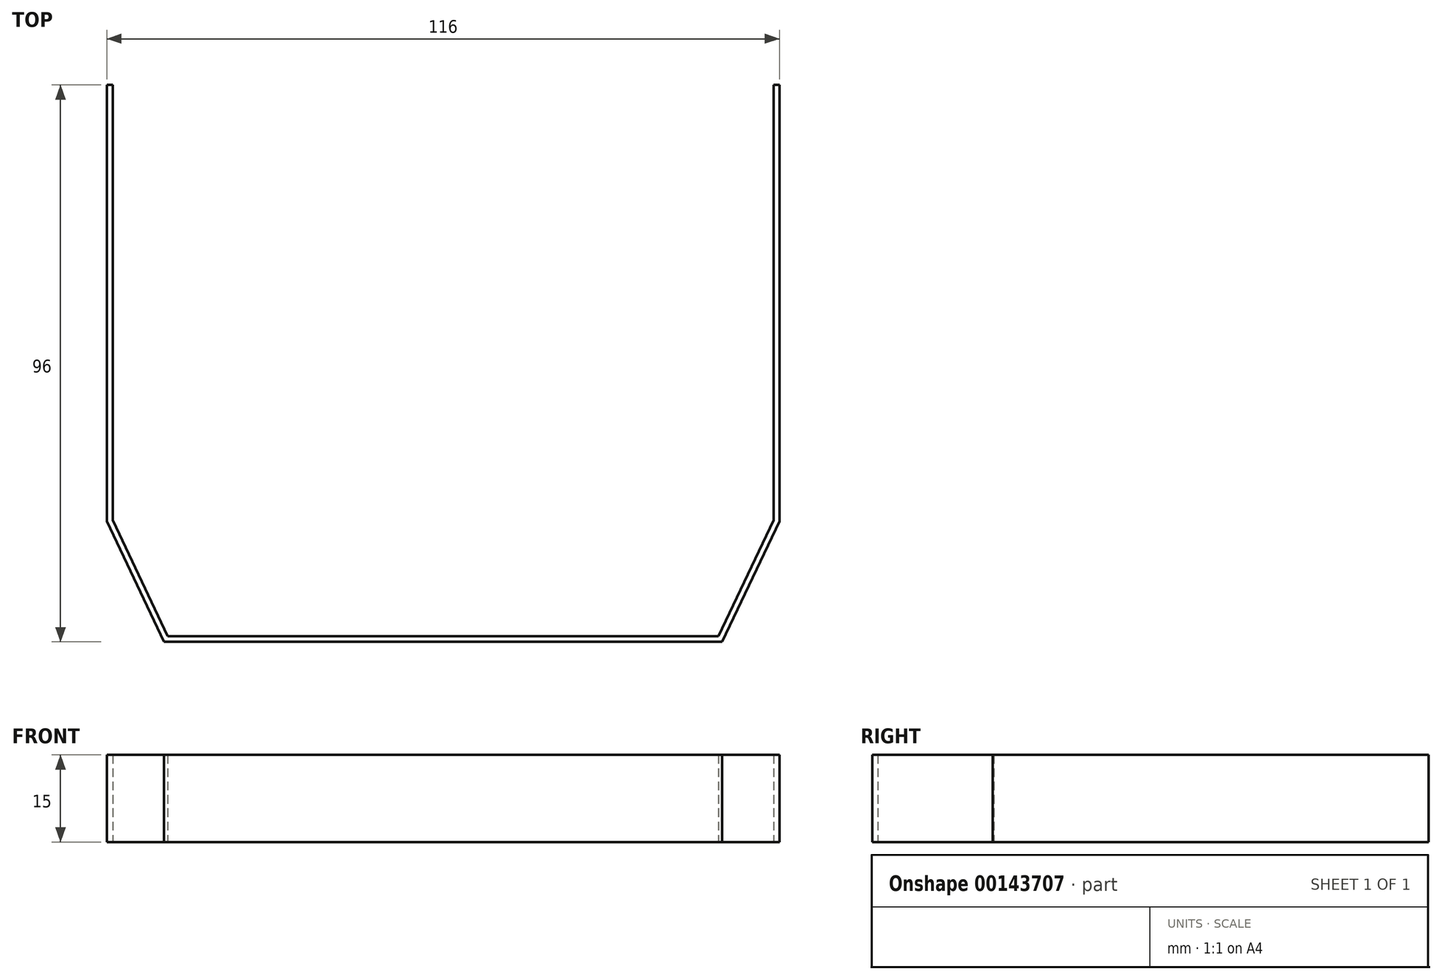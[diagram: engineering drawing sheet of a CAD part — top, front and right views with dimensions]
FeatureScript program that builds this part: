
annotation { "Feature Type Name" : "Feature", "Feature Type Description" : "" }
export const myFeature = defineFeature(function(context is Context, id is Id, definition is map)
    precondition{}
    {
        {
            var Q0;
            Q0=qCreatedBy(makeId("Top.planeOp"),FACE);
            var sketch = newSketch(context, id + "F0", { "sketchPlane" : qUnion([Q0])});
            skLineSegment(sketch, "E0", {"start": v(-57, 46) * mm, "end": v(-57, -29) * mm});
            skLineSegment(sketch, "E1", {"start": v(-57, -29) * mm, "end": v(-47.5, -49) * mm});
            skLineSegment(sketch, "E2", {"start": v(-47.5, -49) * mm, "end": v(47.5, -49) * mm});
            skLineSegment(sketch, "E3", {"start": v(47.5, -49) * mm, "end": v(57, -29) * mm});
            skLineSegment(sketch, "E4", {"start": v(57, -29) * mm, "end": v(57, 46) * mm});
            skLineSegment(sketch, "E5", {"start": v(57, 46) * mm, "end": v(58, 46) * mm});
            skLineSegment(sketch, "E6", {"start": v(58, 46) * mm, "end": v(58, -29.23) * mm});
            skLineSegment(sketch, "E7", {"start": v(58, -29.23) * mm, "end": v(48.13, -50) * mm});
            skLineSegment(sketch, "E8", {"start": v(48.13, -50) * mm, "end": v(-48.13, -50) * mm});
            skLineSegment(sketch, "E9", {"start": v(-48.13, -50) * mm, "end": v(-58, -29.23) * mm});
            skLineSegment(sketch, "E10", {"start": v(-58, -29.23) * mm, "end": v(-58, 46) * mm});
            skLineSegment(sketch, "E11", {"start": v(-58, 46) * mm, "end": v(-57, 46) * mm});
            skSolve(sketch);
        }
        {
            var Q0;
            Q0 = qSketchRegion(id + "F0", true);
            extrude(context, id + "F1", {"entities" : qUnion([Q0]), "depth" : 10 * mm, "hasSecondDirection" : true, "secondDirectionOppositeDirection" : true, "secondDirectionDepth" : 5 * mm});
        }
    });
